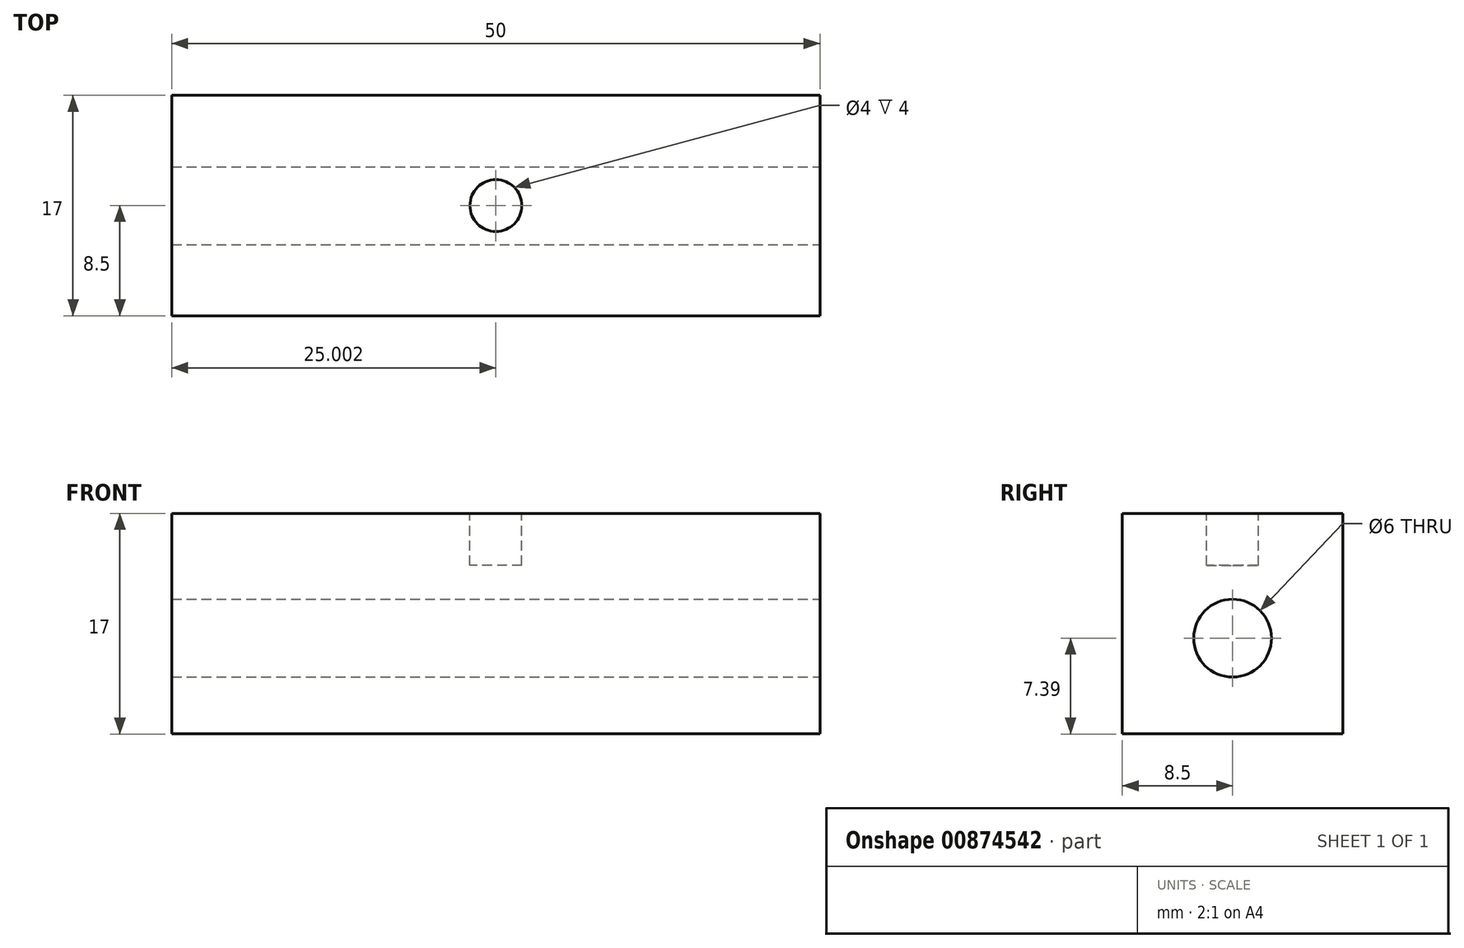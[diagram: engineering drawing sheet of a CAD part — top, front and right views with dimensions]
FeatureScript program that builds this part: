
annotation { "Feature Type Name" : "Feature", "Feature Type Description" : "" }
export const myFeature = defineFeature(function(context is Context, id is Id, definition is map)
    precondition{}
    {
        {
            var Q0;
            Q0=qCreatedBy(makeId("Front.planeOp"),FACE);
            var sketch = newSketch(context, id + "F0", { "sketchPlane" : qUnion([Q0])});
            skLineSegment(sketch, "E0.bottom", {"start": v(-47.6, 9.61) * mm, "end": v(2.4, 9.61) * mm});
            skLineSegment(sketch, "E0.top", {"start": v(-47.6, -7.39) * mm, "end": v(2.4, -7.39) * mm});
            skLineSegment(sketch, "E0.left", {"start": v(-47.6, 9.61) * mm, "end": v(-47.6, -7.39) * mm});
            skLineSegment(sketch, "E0.right", {"start": v(2.4, 9.61) * mm, "end": v(2.4, -7.39) * mm});
            skSolve(sketch);
        }
        {
            var Q0;
            Q0=makeQuery(id+"F0.imprint","IMPRINT",FACE,{"disambiguationData":[TD([[makeQuery(id+"F0.imprint","IMPRINT",EDGE,{"derivedFrom":sQuery(id+"F0.wireOp",EDGE,"E0.bottom")}),-1.0]])]});
            extrude(context, id + "F1", {"entities" : qUnion([Q0]), "depth" : 17 * mm, "offsetDistance" : 25 * mm});
        }
        {
            var Q0;
            Q0=makeQuery(id+"F1.opExtrude","SWEPT_FACE",FACE,{"disambiguationData":[OSD([sQuery(id+"F0.wireOp",EDGE,"E0.right")])]});
            var sketch = newSketch(context, id + "F2", { "sketchPlane" : qUnion([Q0])});
            skCircle(sketch, "E1", {"center": v(-8.5, 0) * mm, "radius": 3 * mm});
            skPoint(sketch, "E1.centerSnap0", {"position": v(-8.5, 9.61) * mm});
            skSolve(sketch);
        }
        {
            var Q0;
            Q0=makeQuery(id+"F2.imprint","IMPRINT",FACE,{"disambiguationData":[TD([[makeQuery(id+"F2.imprint","IMPRINT",EDGE,{"derivedFrom":sQuery(id+"F2.wireOp",EDGE,"E1")}),1.0]])]});
            extrude(context, id + "F3", {"entities" : qUnion([Q0]), "operationType" : NewBodyOperationType.REMOVE, "oppositeDirection" : true, "depth" : 50.1 * mm, "offsetDistance" : 25 * mm});
        }
        {
            var Q0;
            Q0=makeQuery(id+"F1.opExtrude","SWEPT_FACE",FACE,{"disambiguationData":[OSD([sQuery(id+"F0.wireOp",EDGE,"E0.bottom")])]});
            var sketch = newSketch(context, id + "F4", { "sketchPlane" : qUnion([Q0])});
            skCircle(sketch, "E2", {"center": v(-22.6, -8.5) * mm, "radius": 2 * mm});
            skPoint(sketch, "E2.centerSnap0", {"position": v(2.4, -8.5) * mm});
            skPoint(sketch, "E2.centerSnap1", {"position": v(-22.6, 0) * mm});
            skSolve(sketch);
        }
        {
            var Q0;
            Q0=makeQuery(id+"F4.imprint","IMPRINT",FACE,{"disambiguationData":[TD([[makeQuery(id+"F4.imprint","IMPRINT",EDGE,{"derivedFrom":sQuery(id+"F4.wireOp",EDGE,"E2")}),1.0]])]});
            var Q1;
            Q1=sQuery(id+"F4.wireOp",EDGE,"E2");
            extrude(context, id + "F5", {"entities" : qUnion([Q0]), "operationType" : NewBodyOperationType.REMOVE, "surfaceOperationType" : NewSurfaceOperationType.ADD, "surfaceEntities" : qUnion([Q1]), "oppositeDirection" : true, "depth" : 4 * mm, "offsetDistance" : 25 * mm});
        }
    });
